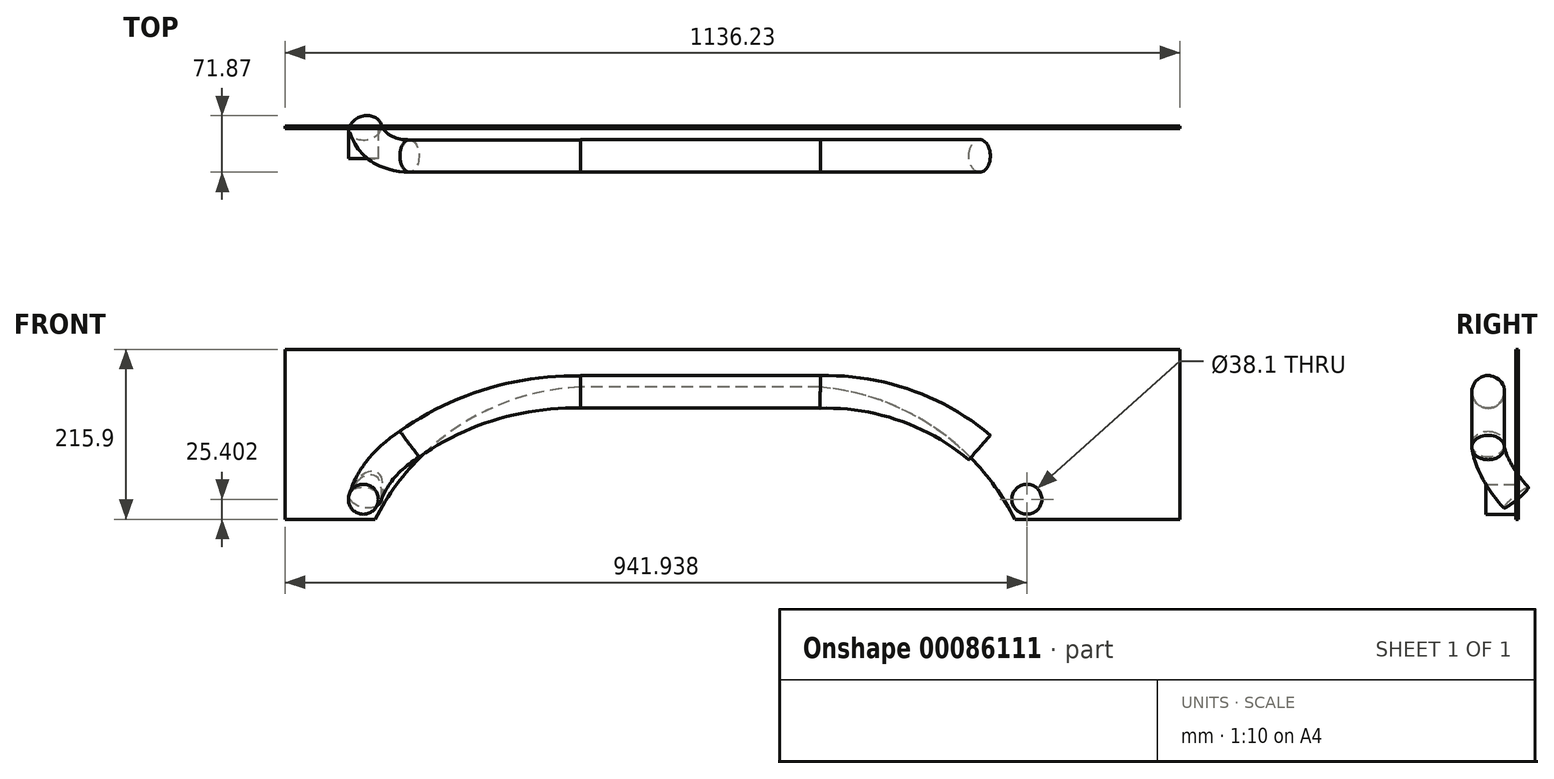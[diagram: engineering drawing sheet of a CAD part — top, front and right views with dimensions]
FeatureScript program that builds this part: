
annotation { "Feature Type Name" : "Feature", "Feature Type Description" : "" }
export const myFeature = defineFeature(function(context is Context, id is Id, definition is map)
    precondition{}
    {
        {
            var Q0;
            Q0=qCreatedBy(makeId("Front.planeOp"),FACE);
            var sketch = newSketch(context, id + "F0", { "sketchPlane" : qUnion([Q0])});
            skLineSegment(sketch, "E0.bottom", {"start": v(-552.54, -103.3) * mm, "end": v(-438.24, -103.3) * mm});
            skLineSegment(sketch, "E0.top", {"start": v(-552.54, 112.6) * mm, "end": v(583.69, 112.6) * mm});
            skLineSegment(sketch, "E0.left", {"start": v(-552.54, -103.3) * mm, "end": v(-552.54, 112.6) * mm});
            skLineSegment(sketch, "E0.right", {"start": v(583.69, -103.3) * mm, "end": v(583.69, 112.6) * mm});
            skLineSegment(sketch, "E1", {"start": v(583.69, -103.3) * mm, "end": v(374.14, -103.3) * mm});
            skLineSegment(sketch, "E2", {"start": v(126.48, 64.54) * mm, "end": v(-178.32, 64.6) * mm});
            skArc(sketch, "E3", {"start": v(-178.32, 64.6) * mm, "mid": v(-331.07, 15.92) * mm, "end": v(-438.24, -103.3) * mm});
            skArc(sketch, "E4", {"start": v(374.14, -103.3) * mm, "mid": v(272.22, 12.95) * mm, "end": v(126.48, 64.54) * mm});
            skLineSegment(sketch, "E5.trimOffspring", {"start": v(374.14, -103.3) * mm, "end": v(583.69, -103.3) * mm});
            skCircle(sketch, "E6", {"center": v(389.4, -77.9) * mm, "radius": 19.05 * mm});
            skLineSegment(sketch, "E7", {"start": v(389.4, -77.9) * mm, "end": v(-453.45, -77.9) * mm, "construction": true});
            skCircle(sketch, "E8", {"center": v(-453.45, -77.9) * mm, "radius": 19.05 * mm});
            skLineSegment(sketch, "E9", {"start": v(-438.24, 64.63) * mm, "end": v(-438.24, -103.3) * mm, "construction": true});
            skLineSegment(sketch, "E10", {"start": v(-438.24, 64.63) * mm, "end": v(-178.32, 64.6) * mm, "construction": true});
            skLineSegment(sketch, "E11", {"start": v(126.48, 64.54) * mm, "end": v(126.48, 112.6) * mm, "construction": true});
            skLineSegment(sketch, "E12", {"start": v(-178.32, 64.6) * mm, "end": v(-178.32, 112.6) * mm, "construction": true});
            skLineSegment(sketch, "E13", {"start": v(374.14, -103.3) * mm, "end": v(374.14, 112.6) * mm, "construction": true});
            skPoint(sketch, "E14", {"position": v(-353.45, 0) * mm});
            skPoint(sketch, "E15", {"position": v(289.93, 0) * mm});
            skSolve(sketch);
        }
        {
            var Q0;
            Q0 = qSketchRegion(id + "F0", true);
            var Q1;
            Q1 = qSketchRegion(id + "F2", true);
            extrude(context, id + "F1", {"entities" : qUnion([Q0, Q1]), "depth" : 3.17 * mm});
        }
        {
            var Q0;
            Q0=qCreatedBy(makeId("Right.planeOp"),FACE);
            var sketch = newSketch(context, id + "F2", { "sketchPlane" : qUnion([Q0])});
            skLineSegment(sketch, "E16", {"start": v(0, 80.67) * mm, "end": v(-38.1, 80.67) * mm, "construction": true});
            skLineSegment(sketch, "E17", {"start": v(-38.1, 80.67) * mm, "end": v(-63.5, 80.67) * mm, "construction": true});
            skCircle(sketch, "E18", {"center": v(-38.1, 58.47) * mm, "radius": 20.7 * mm});
            skSolve(sketch);
        }
        {
            var Q0;
            Q0 = qSketchRegion(id + "F2", true);
            extrude(context, id + "F3", {"entities" : qUnion([Q0]), "oppositeDirection" : true, "depth" : 177.8 * mm});
        }
        {
            var Q0;
            Q0 = qSketchRegion(id + "F2", true);
            extrude(context, id + "F4", {"entities" : qUnion([Q0]), "operationType" : NewBodyOperationType.ADD, "depth" : 127 * mm});
        }
        {
            var Q0;
            Q0=makeQuery(id+"F4.opExtrude","CAP_FACE",FACE,{"disambiguationData":[OSD([sQuery(id+"F2.wireOp",EDGE,"E18")])],"isStart":false});
            var sketch = newSketch(context, id + "F5", { "sketchPlane" : qUnion([Q0])});
            skPoint(sketch, "E19", {"position": v(-38.1, 58.47) * mm});
            skCircle(sketch, "E20", {"center": v(-38.1, 58.47) * mm, "radius": 20.72 * mm});
            skSolve(sketch);
        }
        {
            var Q0;
            Q0=makeQuery(id+"F1.opExtrude","CAP_FACE",FACE,{"disambiguationData":[OSD([sQuery(id+"F0.wireOp",EDGE,"E0.top"),sQuery(id+"F0.wireOp",EDGE,"E0.left"),sQuery(id+"F0.wireOp",EDGE,"E0.right"),sQuery(id+"F0.wireOp",EDGE,"E0.bottom"),sQuery(id+"F0.wireOp",EDGE,"E2"),sQuery(id+"F0.wireOp",EDGE,"E3"),sQuery(id+"F0.wireOp",EDGE,"E4"),sQuery(id+"F0.wireOp",EDGE,"E5.trimOffspring"),sQuery(id+"F0.wireOp",EDGE,"E6"),sQuery(id+"F0.wireOp",EDGE,"E8")])],"isStart":false});
            cPlane(context, id + "F6", {"entities" : qUnion([Q0]), "cplaneType" : CPlaneType.OFFSET, "offset" : 34.3 * mm, "width" : 152.4 * mm, "height" : 152.4 * mm});
        }
        {
            var Q0;
            Q0=qCreatedBy(id+"F6.planeOp",FACE);
            var sketch = newSketch(context, id + "F7", { "sketchPlane" : qUnion([Q0])});
            skPoint(sketch, "E21", {"position": v(126.3, 58.98) * mm});
            skArc(sketch, "E22", {"start": v(329.68, -11.7) * mm, "mid": v(234.44, 42.21) * mm, "end": v(126.3, 58.98) * mm});
            skPoint(sketch, "E23", {"position": v(-178.56, 59.72) * mm});
            skArc(sketch, "E24", {"start": v(-178.56, 59.72) * mm, "mid": v(-292.75, 43.62) * mm, "end": v(-396.2, -7.33) * mm});
            skSolve(sketch);
        }
        {
            var Q0;
            Q0=makeQuery(id+"F3.opExtrude","CAP_FACE",FACE,{"disambiguationData":[OSD([sQuery(id+"F2.wireOp",EDGE,"E18")])],"isStart":false});
            var sketch = newSketch(context, id + "F8", { "sketchPlane" : qUnion([Q0])});
            skCircle(sketch, "E25", {"center": v(38.1, 58.47) * mm, "radius": 20.44 * mm});
            skSolve(sketch);
        }
        {
            var Q0;
            Q0=makeQuery(id+"F8.imprint","IMPRINT",FACE,{"disambiguationData":[TD([[makeQuery(id+"F8.imprint","IMPRINT",EDGE,{"derivedFrom":sQuery(id+"F8.wireOp",EDGE,"E25")}),1.0]])]});
            var Q1;
            Q1=sQuery(id+"F7.wireOp",EDGE,"E24");
            sweep(context, id + "F9", {"operationType" : NewBodyOperationType.ADD, "profiles" : qUnion([Q0]), "path" : qUnion([Q1])});
        }
        {
            var Q0;
            Q0=makeQuery(id+"F5.imprint","IMPRINT",FACE,{"disambiguationData":[TD([[makeQuery(id+"F5.imprint","IMPRINT",EDGE,{"derivedFrom":makeQuery(id+"F4.opExtrude","CAP_EDGE",EDGE,{"disambiguationData":[OSD([sQuery(id+"F2.wireOp",EDGE,"E18")])],"isStart":false})}),1.0]])]});
            var Q1;
            Q1=sQuery(id+"F7.wireOp",EDGE,"E22");
            sweep(context, id + "F10", {"operationType" : NewBodyOperationType.ADD, "profiles" : qUnion([Q0]), "path" : qUnion([Q1])});
        }
        {
            var Q0;
            Q0=sQuery(id+"F7.wireOp",VERTEX,"E24.end");
            var Q1;
            Q1=sQuery(id+"F0.wireOp",VERTEX,"E8.center");
            cPlane(context, id + "F11", {"entities" : qUnion([Q0, Q1]), "cplaneType" : CPlaneType.MID_PLANE, "offset" : 152.4 * mm, "width" : 152.4 * mm, "height" : 152.4 * mm});
        }
        {
            var Q0;
            Q0=qCreatedBy(id+"F11.planeOp",FACE);
            var sketch = newSketch(context, id + "F12", { "sketchPlane" : qUnion([Q0])});
            skCircle(sketch, "E26", {"center": v(-340.43, 43.7) * mm, "radius": 19.28 * mm});
            skSolve(sketch);
        }
        {
            var Q0;
            Q0=sQuery(id+"F0.wireOp",VERTEX,"E8.center");
            var Q1;
            Q1=sQuery(id+"F12.wireOp",VERTEX,"E26.center");
            var Q2;
            Q2=sQuery(id+"F7.wireOp",VERTEX,"E24.end");
            cPlane(context, id + "F13", {"entities" : qUnion([Q0, Q1, Q2]), "cplaneType" : CPlaneType.THREE_POINT, "offset" : 152.4 * mm, "width" : 152.4 * mm, "height" : 152.4 * mm});
        }
        {
            var Q0;
            Q0=qCreatedBy(id+"F13.planeOp",FACE);
            var sketch = newSketch(context, id + "F14", { "sketchPlane" : qUnion([Q0])});
            skArc(sketch, "E27", {"start": v(-373.62, 22.75) * mm, "mid": v(-413.32, -6.53) * mm, "end": v(-434.52, -51.07) * mm});
            skSolve(sketch);
        }
        {
            var Q0;
            Q0=makeQuery(id+"F9.opSweep","CAP_FACE",FACE,{"disambiguationData":[OSD([sQuery(id+"F7.wireOp",VERTEX,"E24.end"),sQuery(id+"F8.wireOp",EDGE,"E25")])],"isStart":false});
            var Q1;
            Q1=makeQuery(id+"F9.opSweep","CAP_EDGE",EDGE,{"disambiguationData":[OSD([sQuery(id+"F7.wireOp",VERTEX,"E24.end"),sQuery(id+"F8.wireOp",EDGE,"E25")])],"isStart":false});
            var Q2;
            Q2=sQuery(id+"F0.wireOp",EDGE,"E8");
            var Q3;
            Q3=sQuery(id+"F14.wireOp",EDGE,"E27");
            sweep(context, id + "F15", {"operationType" : NewBodyOperationType.ADD, "profiles" : qUnion([Q0]), "surfaceProfiles" : qUnion([Q1, Q2]), "path" : qUnion([Q3])});
        }
        {
            var Q0;
            Q0=makeQuery(id+"F0.imprint","IMPRINT",FACE,{"disambiguationData":[TD([[makeQuery(id+"F0.imprint","IMPRINT",EDGE,{"derivedFrom":sQuery(id+"F0.wireOp",EDGE,"E8")}),1.0]])]});
            extrude(context, id + "F16", {"entities" : qUnion([Q0]), "depth" : 41.3 * mm});
        }
        {
            var Q0;
            Q0=makeQuery(id+"F10.opSweep","CAP_FACE",FACE,{"disambiguationData":[OSD([sQuery(id+"F2.wireOp",EDGE,"E18"),sQuery(id+"F7.wireOp",VERTEX,"E22.start")])],"isStart":false});
            cPlane(context, id + "F17", {"entities" : qUnion([Q0]), "cplaneType" : CPlaneType.OFFSET, "offset" : 50.8 * mm, "width" : 152.4 * mm, "height" : 152.4 * mm});
        }
    });
